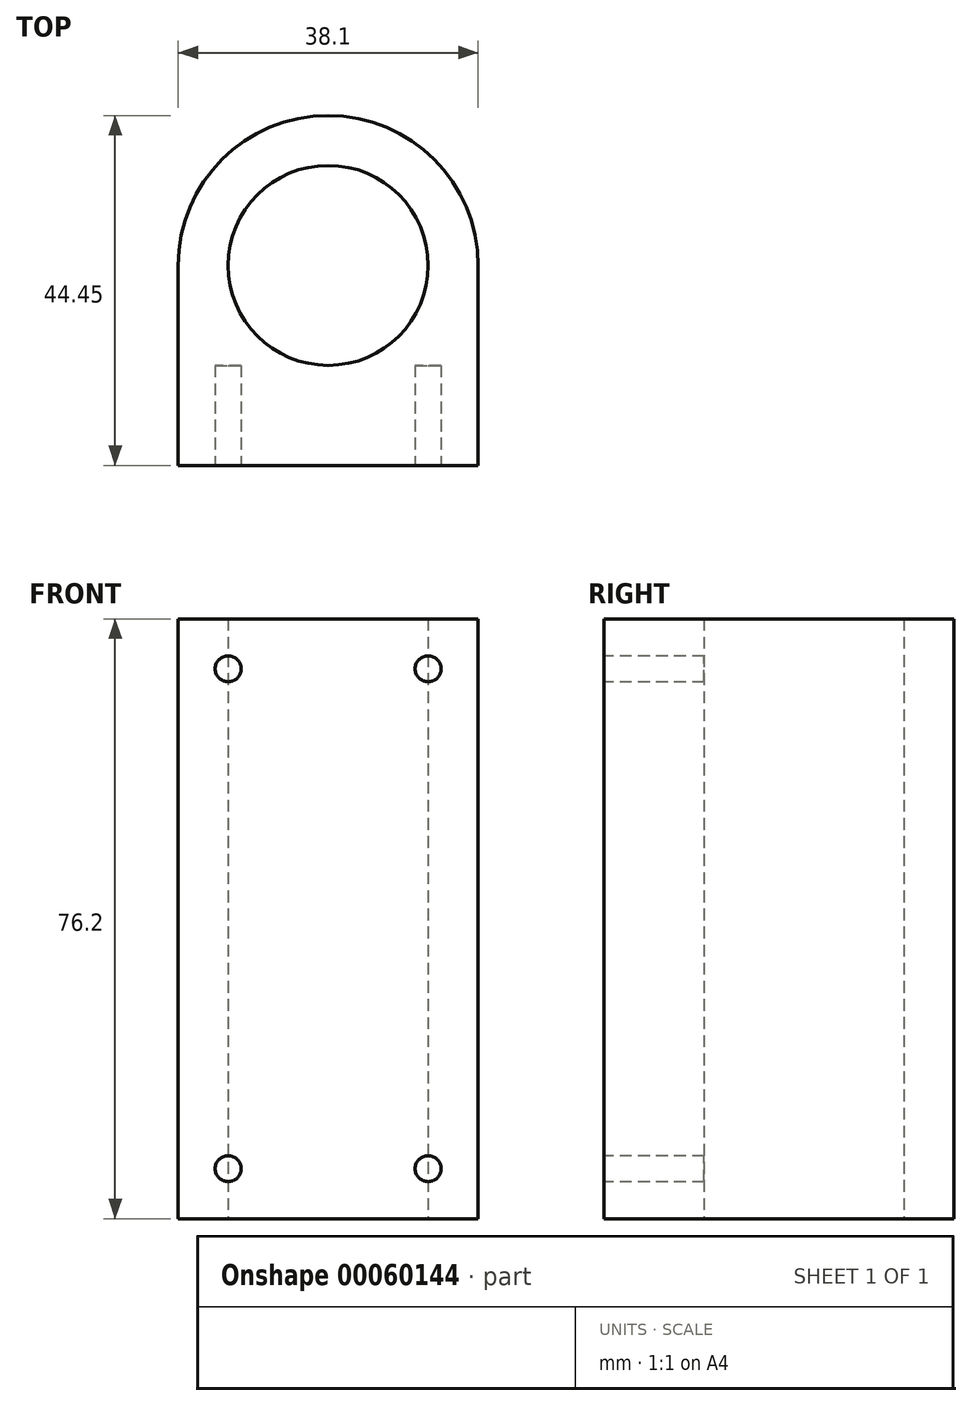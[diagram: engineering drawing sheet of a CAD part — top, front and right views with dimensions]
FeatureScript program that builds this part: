
annotation { "Feature Type Name" : "Feature", "Feature Type Description" : "" }
export const myFeature = defineFeature(function(context is Context, id is Id, definition is map)
    precondition{}
    {
        {
            var Q0;
            Q0=qCreatedBy(makeId("Top.planeOp"),FACE);
            var sketch = newSketch(context, id + "F0", { "sketchPlane" : qUnion([Q0])});
            skCircle(sketch, "E0", {"center": v(0, 0) * mm, "radius": 19.05 * mm});
            skLineSegment(sketch, "E1.bottom", {"start": v(-19.05, 0) * mm, "end": v(19.05, 0) * mm});
            skLineSegment(sketch, "E1.top", {"start": v(-19.05, -25.4) * mm, "end": v(19.05, -25.4) * mm});
            skLineSegment(sketch, "E1.left", {"start": v(-19.05, 0) * mm, "end": v(-19.05, -25.4) * mm});
            skLineSegment(sketch, "E1.right", {"start": v(19.05, 0) * mm, "end": v(19.05, -25.4) * mm});
            skCircle(sketch, "E2", {"center": v(0, 0) * mm, "radius": 12.7 * mm});
            skSolve(sketch);
        }
        {
            var Q0;
            Q0 = qSketchRegion(id + "F0", true);
            var Q1;
            Q1=makeQuery(id+"F0.imprint","IMPRINT",FACE,{"disambiguationData":[TD([[makeQuery(id+"F0.imprint","IMPRINT",EDGE,{"derivedFrom":sQuery(id+"F0.wireOp",EDGE,"E1.top")}),1.0]])]});
            extrude(context, id + "F1", {"entities" : qUnion([Q0, Q1]), "endBound" : BoundingType.SYMMETRIC, "depth" : 76.2 * mm});
        }
        {
            var Q0;
            Q0=makeQuery(id+"F1.opExtrude","SWEPT_FACE",FACE,{"disambiguationData":[OSD([sQuery(id+"F0.wireOp",EDGE,"E1.top")])]});
            var sketch = newSketch(context, id + "F2", { "sketchPlane" : qUnion([Q0])});
            skCircle(sketch, "E3", {"center": v(12.7, 31.75) * mm, "radius": 1.65 * mm});
            skCircle(sketch, "E4", {"center": v(-12.7, 31.75) * mm, "radius": 1.65 * mm});
            skCircle(sketch, "E5", {"center": v(-12.7, -31.75) * mm, "radius": 1.65 * mm});
            skCircle(sketch, "E6", {"center": v(12.7, -31.75) * mm, "radius": 1.65 * mm});
            skSolve(sketch);
        }
        {
            var Q0;
            Q0 = qSketchRegion(id + "F2", true);
            extrude(context, id + "F3", {"entities" : qUnion([Q0]), "operationType" : NewBodyOperationType.REMOVE, "oppositeDirection" : true, "depth" : 12.7 * mm});
        }
    });
